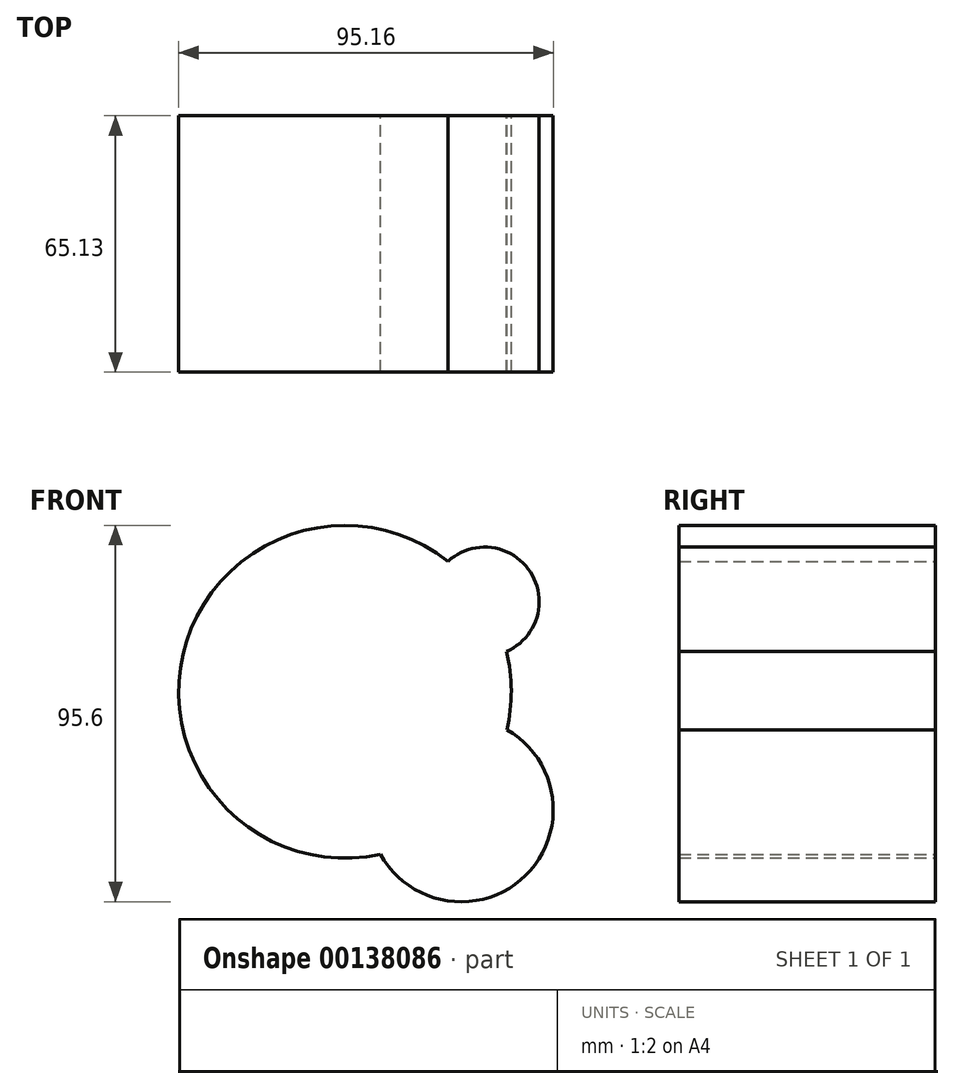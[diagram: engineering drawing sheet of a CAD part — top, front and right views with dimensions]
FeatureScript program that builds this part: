
annotation { "Feature Type Name" : "Feature", "Feature Type Description" : "" }
export const myFeature = defineFeature(function(context is Context, id is Id, definition is map)
    precondition{}
    {
        {
            var Q0;
            Q0=qCreatedBy(makeId("Front.planeOp"),FACE);
            var sketch = newSketch(context, id + "F0", { "sketchPlane" : qUnion([Q0])});
            skArc(sketch, "E0", {"start": v(41.14, -9.64) * mm, "mid": v(42.25, 0.3) * mm, "end": v(41, 10.22) * mm});
            skArc(sketch, "E1", {"start": v(9.02, -41.28) * mm, "mid": v(45.93, -46.62) * mm, "end": v(41.14, -9.64) * mm});
            skArc(sketch, "E2", {"start": v(41, 10.22) * mm, "mid": v(47.12, 30.44) * mm, "end": v(26.17, 33.17) * mm});
            skArc(sketch, "E3.trimOffspring", {"start": v(26.17, 33.17) * mm, "mid": v(-41.17, 9.49) * mm, "end": v(9.02, -41.28) * mm});
            skSolve(sketch);
        }
        {
            var Q0;
            Q0 = qSketchRegion(id + "F0", true);
            extrude(context, id + "F1", {"entities" : qUnion([Q0]), "depth" : 65.13 * mm});
        }
    });
